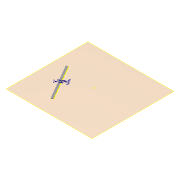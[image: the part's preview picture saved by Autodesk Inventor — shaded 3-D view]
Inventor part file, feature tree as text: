
AUTODESK INVENTOR PART (.ipt)
format: ipt  version: 2014 (Build 180170000, 170)  size: 233,984 bytes
history: native  units: mm
features: extrude x3, sketch x3, reference x2, plane x1, pattern_linear x1, fillet x1
ambient origin geometry x8: Origin, YZ Plane, XZ Plane, XY Plane, X Axis, Y Axis, Z Axis, Center Point
bodies: Solid1 (feature_tree), Solid2 (feature_tree), Solid3 (feature_tree)
feature tree (11):
  plane  "Work Plane1"
  extrude  "Extrusion1"  Depth=5.0mm
  extrude  "Extrusion2"  Depth=2.0mm
  pattern_linear  "Rectangular Pattern1"  Count1=20  [1 undecoded]
  extrude  "Extrusion3"  Depth=50.0mm
  fillet  "Fillet1"  Radius=2.0mm
  sketch  "Sketch1"  dims[d0=1.0mm d1=0.0mm d3=5.0mm]
  reference  "Reference1"
  reference  "Reference2"
  sketch  "Sketch2"  dims[d10=2.0mm d11=2.0mm]
  sketch  "Sketch3"  dims[d12=10.0mm d13=200.0mm d14=50.0mm d15=2.0mm d16=2.0mm d17=2.0mm d18=2.0mm d19=5.0mm d20=5.0mm d23=25.0mm d26=16.66mm d27=16.66mm d28=2.0mm d29=0.0mm d30=40.0mm d32=50.0mm d33=60.0deg d34=1.0mm d35=10.0mm d36=1.0mm d37=60.0deg d38=1.0mm d39=60.0deg d40=1.0mm d41=1.5mm d42=1.5mm d43=10.0mm d44=4.0mm d45=4.0mm d46=10.0mm d47=10.0mm d48=1.0mm d49=0.0mm d50=0.5mm]
note: 1 required parameter value undecoded (feature->parameter linkage not recoverable at this tier; creation-order binding heuristic only, values carry confidence <= 0.55)
